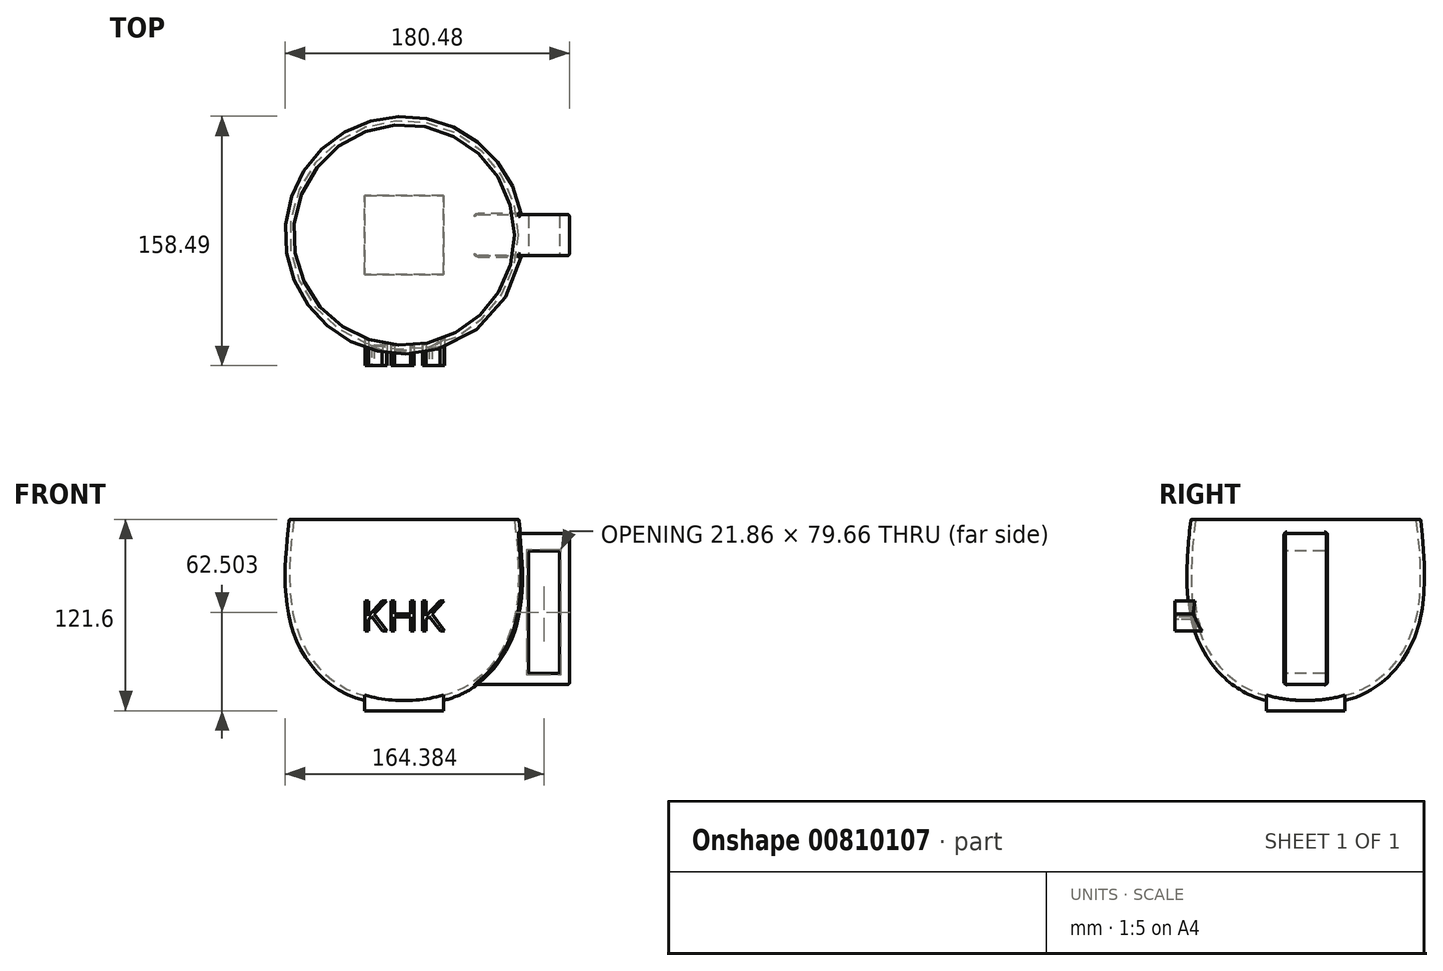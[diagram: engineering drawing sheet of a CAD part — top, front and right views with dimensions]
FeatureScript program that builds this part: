
annotation { "Feature Type Name" : "Feature", "Feature Type Description" : "" }
export const myFeature = defineFeature(function(context is Context, id is Id, definition is map)
    precondition{}
    {
        {
            var Q0;
            Q0=qCreatedBy(makeId("Front.planeOp"),FACE);
            var sketch = newSketch(context, id + "F0", { "sketchPlane" : qUnion([Q0])});
            skFitSpline(sketch, "E0", {"points": [v(72.16, 58.69) * mm, v(71.45, -16.84) * mm, v(36.7, -59.4) * mm, v(-21.1, -66.14) * mm], "startDerivative": vector(24.5, -218.15) * mm, "endDerivative": vector(-191.48, 5.7) * mm});
            skFitSpline(sketch, "E1.0", {"points": [v(69.18, 58.35) * mm, v(70.2, 49.26) * mm, v(71.73, 35.69) * mm, v(72.6, 18.24) * mm, v(72.4, 5.62) * mm, v(71.3, -4.39) * mm, v(69.73, -12.02) * mm, v(68.17, -17.54) * mm, v(66.2, -22.87) * mm, v(63.1, -29.69) * mm, v(58.3, -37.57) * mm, v(52.45, -44.42) * mm, v(47.24, -49.17) * mm, v(43.08, -52.33) * mm, v(39.43, -54.62) * mm, v(36.4, -56.23) * mm, v(33.32, -57.68) * mm, v(29.32, -59.22) * mm, v(22.64, -61.16) * mm, v(13.8, -62.7) * mm, v(2.59, -63.47) * mm, v(-9.07, -63.5) * mm, v(-17.02, -63.26) * mm, v(-21.01, -63.14) * mm]});
            skLineSegment(sketch, "E2", {"start": v(0, 57.98) * mm, "end": v(0, -76.77) * mm});
            skLineSegment(sketch, "E3", {"start": v(56.92, 51.6) * mm, "end": v(93.09, 51.6) * mm});
            skSolve(sketch);
        }
        {
            var Q0;
            {var subQ0=sQuery(id+"F0.wireOp",EDGE,"E2");var subQ1=sQuery(id+"F0.wireOp",EDGE,"E0");var subQ2=makeQuery(id+"F0.imprint","INTERSECT",VERTEX,{"derivedFrom":[subQ1,subQ0]});Q0=makeQuery(id+"F0.imprint","IMPRINT",FACE,{"disambiguationData":[TD([[makeQuery(id+"F0.imprint","IMPRINT",EDGE,{"disambiguationData":[TD([[subQ2,1.0]])],"derivedFrom":subQ1}),-1.0]])]});}
            var Q1;
            Q1=sQuery(id+"F0.wireOp",EDGE,"E2");
            revolve(context, id + "F1", {"surfaceOperationType" : NewSurfaceOperationType.NEW, "entities" : qUnion([Q0]), "axis" : qUnion([Q1]), "revolveType" : RevolveType.FULL});
        }
        {
            var Q0;
            Q0=qCreatedBy(makeId("Front.planeOp"),FACE);
            cPlane(context, id + "F2", {"entities" : qUnion([Q0]), "cplaneType" : CPlaneType.OFFSET, "offset" : 83 * mm, "width" : 150 * mm, "height" : 150 * mm});
        }
        {
            var Q0;
            Q0=qCreatedBy(id+"F2.planeOp",FACE);
            var sketch = newSketch(context, id + "F3", { "sketchPlane" : qUnion([Q0])});
            skText(sketch, "E4", { "text": "KHK", "fontName": "OpenSans-Regular.ttf"});
            const initialGuessF3  = {"E4": [-0.0275, -0.0195, 1, 0, 0.0195]};
            skSetInitialGuess(sketch, initialGuessF3);
            skSolve(sketch);
        }
        {
            var Q0;
            Q0 = qSketchRegion(id + "F3", true);
            extrude(context, id + "F4", {"entities" : qUnion([Q0]), "operationType" : NewBodyOperationType.ADD, "endBound" : BoundingType.UP_TO_NEXT, "oppositeDirection" : true, "depth" : 25 * mm, "offsetDistance" : 25 * mm});
        }
        {
            var Q0;
            Q0=qCreatedBy(makeId("Right.planeOp"),FACE);
            cPlane(context, id + "F5", {"entities" : qUnion([Q0]), "cplaneType" : CPlaneType.OFFSET, "offset" : 105 * mm, "width" : 150 * mm, "height" : 150 * mm});
        }
        {
            var Q0;
            Q0=qCreatedBy(id+"F5.planeOp",FACE);
            var sketch = newSketch(context, id + "F6", { "sketchPlane" : qUnion([Q0])});
            skLineSegment(sketch, "E5.bottom", {"start": v(-13, 42.63) * mm, "end": v(13, 42.63) * mm});
            skLineSegment(sketch, "E5.top", {"start": v(-13, -53.37) * mm, "end": v(13, -53.37) * mm});
            skLineSegment(sketch, "E5.left", {"start": v(-13, 42.63) * mm, "end": v(-13, -53.37) * mm});
            skLineSegment(sketch, "E5.right", {"start": v(13, 42.63) * mm, "end": v(13, -53.37) * mm});
            skSolve(sketch);
        }
        {
            var Q0;
            Q0=makeQuery(id+"F6.imprint","IMPRINT",FACE,{"disambiguationData":[TD([[makeQuery(id+"F6.imprint","IMPRINT",EDGE,{"derivedFrom":sQuery(id+"F6.wireOp",EDGE,"E5.bottom")}),-1.0]])]});
            extrude(context, id + "F7", {"entities" : qUnion([Q0]), "operationType" : NewBodyOperationType.ADD, "endBound" : BoundingType.UP_TO_NEXT, "oppositeDirection" : true, "depth" : 25 * mm, "offsetDistance" : 25 * mm});
        }
        {
            var Q0;
            Q0=makeQuery(id+"F7.opExtrude","SWEPT_FACE",FACE,{"disambiguationData":[OSD([sQuery(id+"F6.wireOp",EDGE,"E5.left")])]});
            var sketch = newSketch(context, id + "F8", { "sketchPlane" : qUnion([Q0])});
            skLineSegment(sketch, "E6.bottom", {"start": v(98.83, 31.33) * mm, "end": v(78.97, 31.33) * mm});
            skLineSegment(sketch, "E6.top", {"start": v(98.83, -46.33) * mm, "end": v(78.97, -46.33) * mm});
            skLineSegment(sketch, "E6.left", {"start": v(98.83, 31.33) * mm, "end": v(98.83, -46.33) * mm});
            skLineSegment(sketch, "E6.right", {"start": v(78.97, 31.33) * mm, "end": v(78.97, -46.33) * mm});
            skSolve(sketch);
        }
        {
            var Q0;
            Q0=makeQuery(id+"F8.imprint","IMPRINT",FACE,{"disambiguationData":[TD([[makeQuery(id+"F8.imprint","IMPRINT",EDGE,{"derivedFrom":sQuery(id+"F8.wireOp",EDGE,"E6.bottom")}),1.0]])]});
            extrude(context, id + "F9", {"entities" : qUnion([Q0]), "operationType" : NewBodyOperationType.REMOVE, "oppositeDirection" : true, "depth" : 50 * mm, "offsetDistance" : 25 * mm});
        }
        {
            var Q0;
            Q0=makeQuery(id+"F7.opExtrude","CAP_FACE",FACE,{"disambiguationData":[OSD([sQuery(id+"F6.wireOp",EDGE,"E5.bottom"),sQuery(id+"F6.wireOp",EDGE,"E5.top"),sQuery(id+"F6.wireOp",EDGE,"E5.left"),sQuery(id+"F6.wireOp",EDGE,"E5.right")])],"isStart":true});
            var Q1;
            Q1=makeQuery(id+"F7.opExtrude","SWEPT_FACE",FACE,{"disambiguationData":[OSD([sQuery(id+"F6.wireOp",EDGE,"E5.bottom")])]});
            var Q2;
            Q2=makeQuery(id+"F7.opExtrude","SWEPT_FACE",FACE,{"disambiguationData":[OSD([sQuery(id+"F6.wireOp",EDGE,"E5.left")])]});
            var Q3;
            Q3=makeQuery(id+"F7.opExtrude","SWEPT_FACE",FACE,{"disambiguationData":[OSD([sQuery(id+"F6.wireOp",EDGE,"E5.right")])]});
            var Q4;
            Q4=makeQuery(id+"F7.opExtrude","SWEPT_FACE",FACE,{"disambiguationData":[OSD([sQuery(id+"F6.wireOp",EDGE,"E5.top")])]});
            var Q5;
            Q5=makeQuery(id+"F9.boolean.opBoolean","COPY",FACE,{"derivedFrom":makeQuery(id+"F9.opExtrude","SWEPT_FACE",FACE,{"disambiguationData":[OSD([sQuery(id+"F8.wireOp",EDGE,"E6.top")])]})});
            var Q6;
            Q6=makeQuery(id+"F9.boolean.opBoolean","COPY",FACE,{"derivedFrom":makeQuery(id+"F9.opExtrude","SWEPT_FACE",FACE,{"disambiguationData":[OSD([sQuery(id+"F8.wireOp",EDGE,"E6.right")])]})});
            var Q7;
            Q7=makeQuery(id+"F9.boolean.opBoolean","COPY",FACE,{"derivedFrom":makeQuery(id+"F9.opExtrude","SWEPT_FACE",FACE,{"disambiguationData":[OSD([sQuery(id+"F8.wireOp",EDGE,"E6.bottom")])]})});
            var Q8;
            Q8=makeQuery(id+"F9.boolean.opBoolean","COPY",FACE,{"derivedFrom":makeQuery(id+"F9.opExtrude","SWEPT_FACE",FACE,{"disambiguationData":[OSD([sQuery(id+"F8.wireOp",EDGE,"E6.left")])]})});
            var Q9;
            Q9=makeQuery(id+"F1.opRevolve","SWEPT_EDGE",EDGE,{"disambiguationData":[OSD([sQuery(id+"F0.wireOp",EDGE,"E0"),sQuery(id+"F0.wireOp",EDGE,"E3")])]});
            var Q10;
            Q10=makeQuery(id+"F1.opRevolve","SWEPT_EDGE",EDGE,{"disambiguationData":[OSD([sQuery(id+"F0.wireOp",EDGE,"E1.0"),sQuery(id+"F0.wireOp",EDGE,"E3")])]});
            fillet(context, id + "F10", {"entities" : qUnion([Q0, Q1, Q2, Q3, Q4, Q5, Q6, Q7, Q8, Q9, Q10]), "radius" : 1 * mm, "tangentPropagation" : true, "allowEdgeOverflow" : false});
        }
        {
            var Q0;
            Q0=qCreatedBy(makeId("Top.planeOp"),FACE);
            cPlane(context, id + "F11", {"entities" : qUnion([Q0]), "cplaneType" : CPlaneType.OFFSET, "offset" : 70 * mm, "oppositeDirection" : true, "width" : 150 * mm, "height" : 150 * mm});
        }
        {
            var Q0;
            Q0=qCreatedBy(id+"F11.planeOp",FACE);
            var sketch = newSketch(context, id + "F12", { "sketchPlane" : qUnion([Q0])});
            skLineSegment(sketch, "E7.bottom", {"start": v(-25, -25) * mm, "end": v(25, -25) * mm});
            skLineSegment(sketch, "E7.top", {"start": v(-25, 25) * mm, "end": v(25, 25) * mm});
            skLineSegment(sketch, "E7.left", {"start": v(-25, -25) * mm, "end": v(-25, 25) * mm});
            skLineSegment(sketch, "E7.right", {"start": v(25, -25) * mm, "end": v(25, 25) * mm});
            skSolve(sketch);
        }
        {
            var Q0;
            Q0=makeQuery(id+"F12.imprint","IMPRINT",FACE,{"disambiguationData":[TD([[makeQuery(id+"F12.imprint","IMPRINT",EDGE,{"derivedFrom":sQuery(id+"F12.wireOp",EDGE,"E7.bottom")}),1.0]])]});
            extrude(context, id + "F13", {"entities" : qUnion([Q0]), "operationType" : NewBodyOperationType.ADD, "endBound" : BoundingType.UP_TO_NEXT, "depth" : 25 * mm, "offsetDistance" : 25 * mm});
        }
    });
